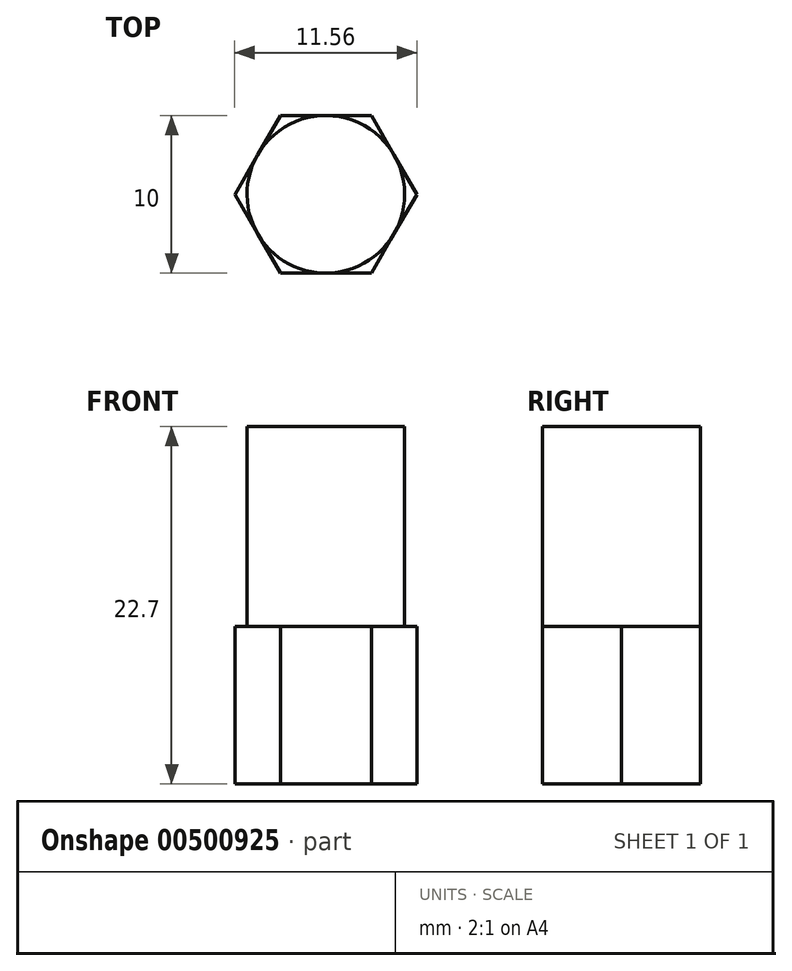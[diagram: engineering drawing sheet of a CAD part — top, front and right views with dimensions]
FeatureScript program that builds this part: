
annotation { "Feature Type Name" : "Feature", "Feature Type Description" : "" }
export const myFeature = defineFeature(function(context is Context, id is Id, definition is map)
    precondition{}
    {
        {
            var Q0;
            Q0=qCreatedBy(makeId("Top.planeOp"),FACE);
            var sketch = newSketch(context, id + "F0", { "sketchPlane" : qUnion([Q0])});
            skCircle(sketch, "E0.cCircle", {"center": v(0, 0) * mm, "radius": 5 * mm, "construction": true});
            skLineSegment(sketch, "E0.0", {"start": v(-2.89, 5) * mm, "end": v(2.89, 5) * mm});
            skLineSegment(sketch, "E0.1", {"start": v(2.89, 5) * mm, "end": v(5.78, 0) * mm});
            skLineSegment(sketch, "E0.2", {"start": v(5.78, 0) * mm, "end": v(2.89, -5) * mm});
            skLineSegment(sketch, "E0.3", {"start": v(2.89, -5) * mm, "end": v(-2.89, -5) * mm});
            skLineSegment(sketch, "E0.4", {"start": v(-2.89, -5) * mm, "end": v(-5.78, 0) * mm});
            skLineSegment(sketch, "E0.5", {"start": v(-5.78, 0) * mm, "end": v(-2.89, 5) * mm});
            skPoint(sketch, "E0.0.midPoint", {"position": v(0, 5) * mm});
            skSolve(sketch);
        }
        {
            var Q0;
            Q0=makeQuery(id+"F0.imprint","IMPRINT",FACE,{"disambiguationData":[TD([[makeQuery(id+"F0.imprint","IMPRINT",EDGE,{"derivedFrom":sQuery(id+"F0.wireOp",EDGE,"E0.0")}),-1.0]])]});
            extrude(context, id + "F1", {"entities" : qUnion([Q0]), "endBound" : BoundingType.SYMMETRIC, "depth" : 10 * mm});
        }
        {
            var Q0;
            Q0=makeQuery(id+"F1.opExtrude","CAP_FACE",FACE,{"disambiguationData":[OSD([sQuery(id+"F0.wireOp",EDGE,"E0.0"),sQuery(id+"F0.wireOp",EDGE,"E0.1"),sQuery(id+"F0.wireOp",EDGE,"E0.2"),sQuery(id+"F0.wireOp",EDGE,"E0.3"),sQuery(id+"F0.wireOp",EDGE,"E0.4"),sQuery(id+"F0.wireOp",EDGE,"E0.5")])],"isStart":false});
            var sketch = newSketch(context, id + "F2", { "sketchPlane" : qUnion([Q0])});
            skCircle(sketch, "E1", {"center": v(0, 0) * mm, "radius": 5 * mm});
            skSolve(sketch);
        }
        {
            var Q0;
            {var subQ0=sQuery(id+"F2.wireOp",EDGE,"E1");var subQ4=makeQuery(id+"F2.imprint","INTERSECT",VERTEX,{"derivedFrom":[makeQuery(id+"F1.opExtrude","CAP_EDGE",EDGE,{"disambiguationData":[OSD([sQuery(id+"F0.wireOp",EDGE,"E0.0")])],"isStart":false}),subQ0]});Q0=makeQuery(id+"F2.imprint","IMPRINT",FACE,{"disambiguationData":[TD([[makeQuery(id+"F2.imprint","IMPRINT",EDGE,{"disambiguationData":[TD([[subQ4,1.0]])],"derivedFrom":subQ0}),1.0]])]});}
            extrude(context, id + "F3", {"entities" : qUnion([Q0]), "operationType" : NewBodyOperationType.ADD, "depth" : 12.7 * mm});
        }
    });
